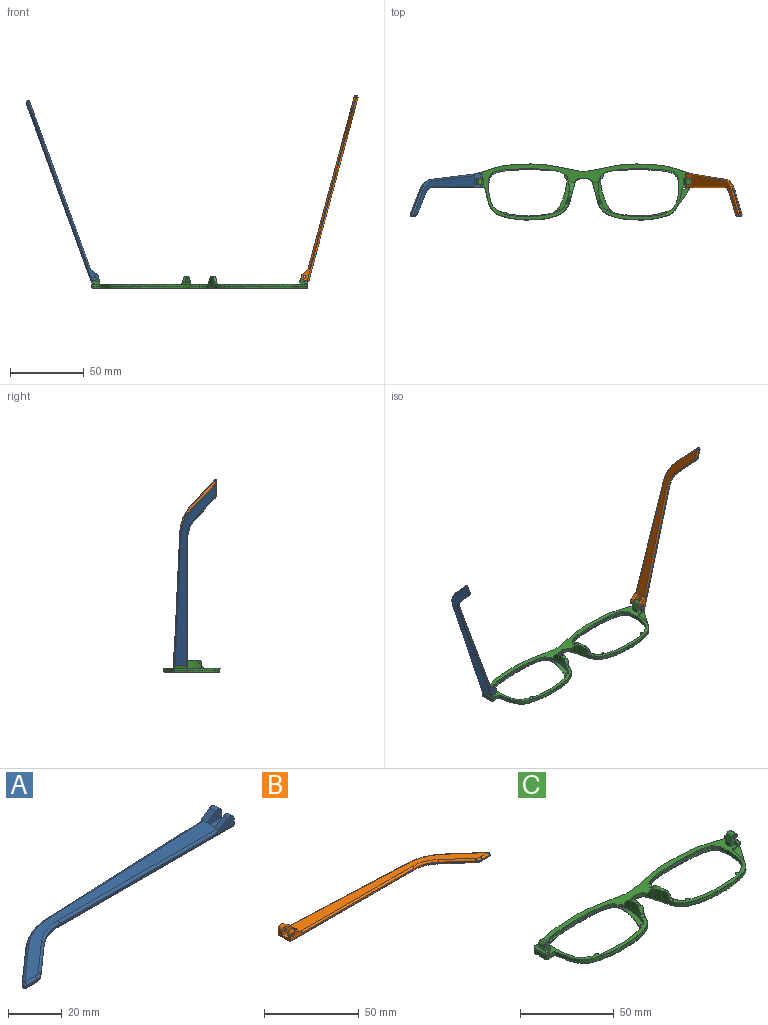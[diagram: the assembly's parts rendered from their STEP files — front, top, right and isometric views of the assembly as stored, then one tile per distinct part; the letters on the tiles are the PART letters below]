
ASSEMBLY  parts=3 mates=2
PART A: 43 faces, bbox 130.2x29.5x5.9 mm
  f0: plane 9.62x3.72mm, normal (1,0,0), area 24.7mm2, adj f1,f3,f4,f5,f10,f16,f18,f28
  f1: cylinder r=2.2mm len=3.45mm, axis (0,-1,0), area 11mm2, adj f0,f2,f4,f37
  f2: plane 6.01x3.91mm, normal (-0.55,0,0.84), area 12.7mm2, adj f1,f4,f9,f19,f37
  f3: plane 2.26x0.1mm, normal (0,0,1), area 0.1mm2, adj f0,f5,f18
  f4: plane 92.1x4.9mm, normal (0,-1,0), area 79.9mm2, adj f0,f1,f2,f14,f19,f36,f42
  f5: plane 93.42x4.13mm, normal (-0.04,1,0), area 64.8mm2, adj f0,f3,f11,f15,f17,f27,f28
  f6: plane 17.82x15.72mm, normal (-0.66,0.75,0), area 14.3mm2, adj f11,f12,f25,f30
  f7: plane 5.46x0.6mm, normal (0,-1,0), area 3.3mm2, adj f12,f13,f23,f32
  f8: plane 14.99x13.23mm, normal (0.66,-0.75,0), area 12mm2, adj f13,f14,f21,f34
  f9: plane 121.18x26.73mm, normal (0,0,1), area 627.7mm2, adj f2,f17,f19,f20,f21,f22,f23,f25
  f10: plane 129.1x27.08mm, normal (0,0,-1), area 686.5mm2, adj f0,f28,f29,f30,f32,f33,f34,f35
  f11: cylinder r=30mm len=18.52mm, axis (0,0,-1), area 12.2mm2, adj f5,f6,f26,f29
  f12: cylinder r=1mm len=1.75mm, axis (0,0,-1), area 1.5mm2, adj f6,f7,f24,f31
  f13: cylinder r=5mm len=3.31mm, axis (0,0,-1), area 2.2mm2, adj f7,f8,f22,f33
  f14: cylinder r=20mm len=13.23mm, axis (0,0,1), area 8.7mm2, adj f4,f8,f20,f35
  f15: plane 5.66x0.25mm, normal (0,0,-1), area 0.7mm2, adj f5,f17,f18
  f16: cylinder r=2.2mm len=3.45mm, axis (0,-1,0), area 14.8mm2, adj f0,f17,f18,f38
  f17: plane 6.01x3.91mm, normal (-0.55,0,0.84), area 16.9mm2, adj f5,f9,f15,f16,f18,f27,f38
  f18: plane 7.92x3.3mm, normal (0,1,0), area 15.9mm2, adj f0,f3,f15,f16,f17,f41
  f19: cylinder r=1mm len=84.18mm, axis (-1,0,0), area 131.4mm2, adj f2,f4,f9,f20
  f20: torus R=21mm, axis (0,0,1), area 23.1mm2, adj f9,f14,f19,f21
  f21: cylinder r=1mm len=15.65mm, axis (-0.75,-0.66,0), area 31.4mm2, adj f8,f9,f20,f22
  f22: torus R=4mm, axis (0,0,1), area 5.3mm2, adj f9,f13,f21,f23
  f23: cylinder r=1mm len=5.46mm, axis (-1,0,0), area 8.6mm2, adj f7,f9,f22,f24
  f24: sphere r=1mm, area 2.4mm2, adj f12,f23,f25
  f25: cylinder r=1mm len=18.48mm, axis (0.75,0.66,0), area 37.3mm2, adj f6,f9,f24,f26
  f26: torus R=29mm, axis (0,0,1), area 31.6mm2, adj f9,f11,f25,f27
  f27: cylinder r=1mm len=85.5mm, axis (1,0.04,0), area 133.5mm2, adj f5,f9,f17,f26
  f28: cylinder r=1mm len=93.46mm, axis (-1,-0.04,0), area 146.9mm2, adj f0,f5,f10,f29
  f29: torus R=29mm, axis (0,0,1), area 31.6mm2, adj f10,f11,f28,f30
  f30: cylinder r=1mm len=18.48mm, axis (-0.75,-0.66,0), area 37.3mm2, adj f6,f10,f29,f31
  f31: sphere r=1mm, area 2.4mm2, adj f12,f30,f32
  f32: cylinder r=1mm len=5.46mm, axis (1,0,0), area 8.6mm2, adj f7,f10,f31,f33
  f33: torus R=4mm, axis (0,0,1), area 5.3mm2, adj f10,f13,f32,f34
  f34: cylinder r=1mm len=15.65mm, axis (0.75,0.66,0), area 31.4mm2, adj f8,f10,f33,f35
  f35: torus R=21mm, axis (0,0,1), area 23.1mm2, adj f10,f14,f34,f36
  f36: cylinder r=1mm len=92.1mm, axis (1,0,0), area 144.7mm2, adj f0,f4,f10,f35
  f37: plane 7.92x4.7mm, normal (0,1,0), area 27mm2, adj f0,f1,f2,f39,f40,f42
  f38: plane 7.92x4.7mm, normal (0,-1,0), area 27mm2, adj f0,f16,f17,f39,f40,f41
  f39: plane 7.92x4.1mm, normal (0,0,1), area 32.5mm2, adj f0,f37,f38,f40
  f40: plane 4.1x1.4mm, normal (1,0,0), area 5.7mm2, adj f9,f37,f38,f39
  f41: cylinder r=0.5mm len=3.1mm, axis (0,-1,0), area 9.7mm2, adj f18,f38
  f42: cylinder r=0.5mm len=2.3mm, axis (0,-1,0), area 7.2mm2, adj f4,f37
PART B: 43 faces, bbox 130.2x29.5x5.9 mm
  f0: plane 9.62x3.72mm, normal (-1,0,0), area 24.7mm2, adj f1,f3,f4,f5,f10,f16,f18,f28
  f1: cylinder r=2.2mm len=3.45mm, axis (0,-1,0), area 11mm2, adj f0,f2,f4,f37
  f2: plane 6.01x3.91mm, normal (0.55,0,0.84), area 12.7mm2, adj f1,f4,f9,f19,f37
  f3: plane 2.26x0.1mm, normal (0,0,1), area 0.1mm2, adj f0,f5,f18
  f4: plane 92.1x4.9mm, normal (0,-1,0), area 78.2mm2, adj f0,f1,f2,f14,f19,f36,f42
  f5: plane 93.42x4.13mm, normal (0.04,1,0), area 64.8mm2, adj f0,f3,f11,f15,f17,f27,f28
  f6: plane 17.82x15.72mm, normal (0.66,0.75,0), area 14.3mm2, adj f11,f12,f25,f30
  f7: plane 5.46x0.6mm, normal (0,-1,0), area 3.3mm2, adj f12,f13,f23,f32
  f8: plane 14.99x13.23mm, normal (-0.66,-0.75,0), area 12mm2, adj f13,f14,f21,f34
  f9: plane 121.18x26.73mm, normal (0,0,1), area 627.7mm2, adj f2,f17,f19,f20,f21,f22,f23,f25
  f10: plane 129.1x27.08mm, normal (0,0,-1), area 686.5mm2, adj f0,f28,f29,f30,f32,f33,f34,f35
  f11: cylinder r=30mm len=18.52mm, axis (0,0,-1), area 12.2mm2, adj f5,f6,f26,f29
  f12: cylinder r=1mm len=1.75mm, axis (0,0,-1), area 1.5mm2, adj f6,f7,f24,f31
  f13: cylinder r=5mm len=3.31mm, axis (0,0,-1), area 2.2mm2, adj f7,f8,f22,f33
  f14: cylinder r=20mm len=13.23mm, axis (0,0,1), area 8.7mm2, adj f4,f8,f20,f35
  f15: plane 5.66x0.25mm, normal (0,0,-1), area 0.7mm2, adj f5,f17,f18
  f16: cylinder r=2.2mm len=3.45mm, axis (0,-1,0), area 14.8mm2, adj f0,f17,f18,f38
  f17: plane 6.01x3.91mm, normal (0.55,0,0.84), area 16.9mm2, adj f5,f9,f15,f16,f18,f27,f38
  f18: plane 7.92x3.3mm, normal (0,1,0), area 14.3mm2, adj f0,f3,f15,f16,f17,f41
  f19: cylinder r=1mm len=84.18mm, axis (1,0,0), area 131.4mm2, adj f2,f4,f9,f20
  f20: torus R=21mm, axis (0,0,1), area 23.1mm2, adj f9,f14,f19,f21
  f21: cylinder r=1mm len=15.65mm, axis (0.75,-0.66,0), area 31.4mm2, adj f8,f9,f20,f22
  f22: torus R=4mm, axis (0,0,1), area 5.3mm2, adj f9,f13,f21,f23
  f23: cylinder r=1mm len=5.46mm, axis (1,0,0), area 8.6mm2, adj f7,f9,f22,f24
  f24: sphere r=1mm, area 2.4mm2, adj f12,f23,f25
  f25: cylinder r=1mm len=18.48mm, axis (-0.75,0.66,0), area 37.3mm2, adj f6,f9,f24,f26
  f26: torus R=29mm, axis (0,0,1), area 31.6mm2, adj f9,f11,f25,f27
  f27: cylinder r=1mm len=85.5mm, axis (-1,0.04,0), area 133.5mm2, adj f5,f9,f17,f26
  f28: cylinder r=1mm len=93.46mm, axis (1,-0.04,0), area 146.9mm2, adj f0,f5,f10,f29
  f29: torus R=29mm, axis (0,0,1), area 31.6mm2, adj f10,f11,f28,f30
  f30: cylinder r=1mm len=18.48mm, axis (0.75,-0.66,0), area 37.3mm2, adj f6,f10,f29,f31
  f31: sphere r=1mm, area 2.4mm2, adj f12,f30,f32
  f32: cylinder r=1mm len=5.46mm, axis (-1,0,0), area 8.6mm2, adj f7,f10,f31,f33
  f33: torus R=4mm, axis (0,0,1), area 5.3mm2, adj f10,f13,f32,f34
  f34: cylinder r=1mm len=15.65mm, axis (-0.75,0.66,0), area 31.4mm2, adj f8,f10,f33,f35
  f35: torus R=21mm, axis (0,0,1), area 23.1mm2, adj f10,f14,f34,f36
  f36: cylinder r=1mm len=92.1mm, axis (-1,0,0), area 144.7mm2, adj f0,f4,f10,f35
  f37: plane 7.92x4.7mm, normal (0,1,0), area 25.4mm2, adj f0,f1,f2,f39,f40,f42
  f38: plane 7.92x4.7mm, normal (0,-1,0), area 25.4mm2, adj f0,f16,f17,f39,f40,f41
  f39: plane 7.92x4.1mm, normal (0,0,1), area 32.5mm2, adj f0,f37,f38,f40
  f40: plane 4.1x1.4mm, normal (-1,0,0), area 5.7mm2, adj f9,f37,f38,f39
  f41: cylinder r=0.88mm len=3.1mm, axis (0,-1,0), area 17mm2, adj f18,f38
  f42: cylinder r=0.88mm len=2.3mm, axis (0,-1,0), area 12.6mm2, adj f4,f37
PART C: 116 faces, bbox 148.1x38.6x17.8 mm
  f0: plane 9.74x2.07mm, normal (0,0,1), area 0.2mm2, adj f1,f115
  f1: extruded ~54.55x32.6mm, area 138.1mm2, adj f0,f2,f103,f104,f105,f106,f107,f108
  f2: extruded ~54.55x32.6mm, area 127.7mm2, adj f1,f3,f103
  f3: plane 54.78x32.76mm, normal (0,0,1), area 120.4mm2, adj f2,f4
  f4: bspline ~55.13x33.28mm, area 230.1mm2, adj f3,f5,f102,f103
  f5: bspline ~72.92x29.28mm, area 158.8mm2, adj f4,f6,f69,f101,f102
  f6: bspline ~72.92x29.28mm, area 158.8mm2, adj f5,f7,f67,f68,f102
  f7: extruded ~73.28x38.08mm, area 259.3mm2, adj f6,f8,f9,f10,f29,f30,f31,f32
  f8: extruded ~0.11x0.03mm, area 0mm2, adj f7,f66
  f9: extruded ~4.12x1.97mm, area 6.9mm2, adj f7,f66
  f10: plane 5.35x2.29mm, normal (0,0,1), area 6.4mm2, adj f7,f11,f28,f29,f66
  f11: bspline ~7.24x7.24mm, area 12.1mm2, adj f10,f12,f27,f28,f29,f30
  f12: bspline ~3.15x1.97mm, area 4.7mm2, adj f11,f13,f14,f31,f112
  f13: cylinder r=1.54mm len=1.03mm, axis (1,0,0), area 0.1mm2, adj f12,f27,f30
  f14: extruded ~54.55x32.6mm, area 138.1mm2, adj f12,f15,f17,f18,f19,f20,f21,f22
  f15: extruded ~54.55x32.6mm, area 127.7mm2, adj f14,f16,f17
  f16: plane 54.78x32.76mm, normal (0,0,1), area 120.4mm2, adj f15,f67
  f17: extruded ~18.85x7.36mm, area 43.3mm2, adj f14,f15,f67,f112
  f18: plane 1.82x1.47mm, normal (0,0,-1), area 1.5mm2, adj f14,f19
  f19: cylinder r=1mm len=1.82mm, axis (0,0,1), area 1.5mm2, adj f14,f18,f112
  f20: plane 3.16x2.48mm, normal (0,0,-1), area 4.2mm2, adj f14,f21
  f21: cylinder r=2mm len=3.15mm, axis (0,0,1), area 2.4mm2, adj f14,f20,f112
  f22: plane 9.74x2.07mm, normal (0,0,1), area 0.2mm2, adj f14,f28
  f23: plane 2.48x1.81mm, normal (0,0,-1), area 2.6mm2, adj f14,f24
  f24: cylinder r=1.3mm len=2.47mm, axis (0,0,1), area 2mm2, adj f14,f23,f112
  f25: plane 2.52x1.67mm, normal (0,0,-1), area 2.6mm2, adj f14,f26
  f26: cylinder r=1.3mm len=2.51mm, axis (0,0,1), area 2mm2, adj f14,f25,f112
  f27: plane 0.42x0.26mm, normal (0,-1,0), area 0mm2, adj f11,f13,f30
  f28: extruded ~9.47x5mm, area 42.8mm2, adj f10,f11,f14,f22,f66
  f29: extruded ~5x4.22mm, area 20.5mm2, adj f7,f10,f11,f30
  f30: bspline ~2.15x0.76mm, area 0.4mm2, adj f7,f11,f13,f27,f29,f31
  f31: bspline ~1.76x0.83mm, area 0.4mm2, adj f7,f12,f30,f32
  f32: bspline ~62.39x22.31mm, area 24.4mm2, adj f7,f31,f33,f112
  f33: plane 2.36x2.31mm, normal (1,0,0), area 4.9mm2, adj f7,f32,f34,f50,f51,f52,f112
  f34: plane 2.76x2.53mm, normal (0,-1,0), area 3.9mm2, adj f33,f35,f49,f50,f53
  f35: cone r=1mm half-angle=20deg, axis (0,0,1), area 2.3mm2, adj f34,f36,f49,f112
  f36: plane 7.67x1.6mm, normal (-0.94,0,-0.34), area 13mm2, adj f35,f37,f49,f112
  f37: cylinder r=1mm len=2.28mm, axis (0.34,0,-0.94), area 3mm2, adj f36,f38,f49,f112
  f38: plane 2.1x1.68mm, normal (0,1,0), area 2.8mm2, adj f37,f39,f49,f50,f112
  f39: plane 3.3x2.1mm, normal (1,0,0), area 6.9mm2, adj f38,f40,f50,f112
  f40: plane 6.97x5.07mm, normal (0,1,0), area 22.7mm2, adj f39,f41,f42,f43,f44,f45,f46,f47
  f41: cylinder r=1.98mm len=4mm, axis (0,1,0), area 12.4mm2, adj f40,f42,f47,f51
  f42: plane 4x0.01mm, normal (-0.34,0,0.94), area 0.1mm2, adj f40,f41,f43,f51
  f43: cylinder r=1.98mm len=4mm, axis (0,-1,0), area 12.4mm2, adj f40,f42,f44,f51
  f44: plane 4x2.21mm, normal (-0.94,0,-0.34), area 9.4mm2, adj f40,f43,f50,f51
  f45: plane 4x2.36mm, normal (1,0,0), area 9.5mm2, adj f40,f46,f52,f112
  f46: plane 4x0.02mm, normal (-0.34,0,0.94), area 0.1mm2, adj f40,f45,f47
  f47: plane 4x3.31mm, normal (0.94,0,0.34), area 14.1mm2, adj f40,f41,f46,f51
  f48: cylinder r=0.88mm len=4mm, axis (0,-1,0), area 22mm2, adj f40,f51
  f49: plane 9.71x1.44mm, normal (-0.34,0,0.94), area 13.9mm2, adj f34,f35,f36,f37,f38,f50
  f50: plane 9.65x1.24mm, normal (0,0,1), area 8.2mm2, adj f33,f34,f38,f39,f40,f44,f49,f51
  f51: plane 5.77x5.07mm, normal (0,-1,0), area 17mm2, adj f33,f41,f42,f43,f44,f47,f48,f50
  f52: plane 3.2x2.36mm, normal (0,-1,0), area 5.7mm2, adj f33,f45,f51,f112
  f53: plane 1.22x0.04mm, normal (0,0,1), area 0mm2, adj f7,f34,f112
  f54: extruded ~35.98x5.06mm, area 72.9mm2, adj f7,f55,f60,f112
  f55: bspline ~38.4x6.08mm, area 57.2mm2, adj f54,f56,f61,f102
  f56: bspline ~38.4x6.08mm, area 57.2mm2, adj f55,f57,f60,f102
  f57: bspline ~44.95x7.5mm, area 58.9mm2, adj f56,f58,f69,f102
  f58: bspline ~1.05x1mm, area 0.7mm2, adj f57,f59,f69
  f59: bspline ~8.77x1.22mm, area 12.6mm2, adj f58,f69,f101,f102
  f60: extruded ~35.98x5.06mm, area 72.9mm2, adj f54,f56,f69,f112
  f61: bspline ~44.95x7.5mm, area 58.9mm2, adj f7,f55,f62,f102
  f62: bspline ~1.05x1mm, area 0.8mm2, adj f7,f61,f63
  f63: bspline ~8.77x1.22mm, area 12.6mm2, adj f7,f62,f68,f102
  f64: bspline ~6.56x3.87mm, area 2.3mm2, adj f7,f65,f66,f112
  f65: bspline ~6.56x3.87mm, area 2.3mm2, adj f64,f69,f108,f112
  f66: bspline ~15.41x15.33mm, area 32.8mm2, adj f7,f8,f9,f10,f14,f28,f64,f112
  f67: bspline ~55.13x33.28mm, area 230.1mm2, adj f6,f16,f17,f102
  f68: bspline ~1x1mm, area 0.8mm2, adj f6,f7,f63
  f69: extruded ~73.28x38.08mm, area 259.3mm2, adj f5,f7,f57,f58,f59,f60,f65,f70
  f70: extruded ~4.12x1.97mm, area 6.9mm2, adj f69,f108
  f71: plane 5.35x2.29mm, normal (0,0,1), area 6.4mm2, adj f69,f72,f75,f108,f115
  f72: bspline ~7.24x7.24mm, area 12.1mm2, adj f71,f73,f75,f76,f109,f115
  f73: plane 0.42x0.26mm, normal (0,-1,0), area 0mm2, adj f72,f74,f76
  f74: cylinder r=1.54mm len=1.03mm, axis (-1,0,0), area 0.1mm2, adj f73,f76,f109
  f75: extruded ~5x4.22mm, area 20.5mm2, adj f69,f71,f72,f76
  f76: bspline ~2.15x0.76mm, area 0.4mm2, adj f69,f72,f73,f74,f75,f77
  f77: bspline ~1.76x0.83mm, area 0.4mm2, adj f69,f76,f78,f109
  f78: bspline ~62.39x22.31mm, area 24.4mm2, adj f69,f77,f79,f112
  f79: plane 2.36x2.31mm, normal (-1,0,0), area 4.9mm2, adj f69,f78,f80,f96,f97,f98,f112
  f80: plane 3.2x2.36mm, normal (0,-1,0), area 5.7mm2, adj f79,f81,f96,f112
  f81: plane 4x2.36mm, normal (-1,0,0), area 9.5mm2, adj f80,f82,f95,f112
  f82: plane 6.97x5.07mm, normal (0,1,0), area 22.7mm2, adj f81,f83,f89,f90,f91,f92,f93,f94
  f83: plane 3.3x2.1mm, normal (-1,0,0), area 6.9mm2, adj f82,f84,f97,f112
  f84: plane 2.1x1.68mm, normal (0,1,0), area 2.8mm2, adj f83,f85,f88,f97,f112
  f85: cylinder r=1mm len=2.28mm, axis (-0.34,0,-0.94), area 3mm2, adj f84,f86,f88,f112
  f86: plane 7.67x1.6mm, normal (0.94,0,-0.34), area 13mm2, adj f85,f87,f88,f112
  f87: cone r=1mm half-angle=20deg, axis (0,0,1), area 2.3mm2, adj f86,f88,f98,f112
  f88: plane 9.71x1.44mm, normal (0.34,0,0.94), area 13.9mm2, adj f84,f85,f86,f87,f97,f98
  f89: plane 4x2.21mm, normal (0.94,0,-0.34), area 9.4mm2, adj f82,f90,f96,f97
  f90: cylinder r=1.98mm len=4mm, axis (0,-1,0), area 12.4mm2, adj f82,f89,f91,f96
  f91: plane 4x0.01mm, normal (0.34,0,0.94), area 0.1mm2, adj f82,f90,f92,f96
  f92: cylinder r=1.98mm len=4mm, axis (0,1,0), area 12.4mm2, adj f82,f91,f93,f96
  f93: plane 4x3.31mm, normal (-0.94,0,0.34), area 14.1mm2, adj f82,f92,f95,f96
  f94: cylinder r=0.88mm len=4mm, axis (0,-1,0), area 22mm2, adj f82,f96
  f95: plane 4x0.02mm, normal (0.34,0,0.94), area 0.1mm2, adj f81,f82,f93
  f96: plane 5.77x5.06mm, normal (0,-1,0), area 17mm2, adj f79,f80,f89,f90,f91,f92,f93,f94
  f97: plane 9.65x1.24mm, normal (0,0,1), area 8.2mm2, adj f79,f82,f83,f84,f88,f89,f96,f98
  f98: plane 2.76x2.53mm, normal (0,-1,0), area 3.9mm2, adj f79,f87,f88,f97,f99
  f99: plane 1.22x0.04mm, normal (0,0,1), area 0mm2, adj f69,f98,f112
  f100: extruded ~0.11x0.03mm, area 0mm2, adj f69,f108
  f101: bspline ~1x1mm, area 0.8mm2, adj f5,f59,f69
  f102: plane 144.79x36.11mm, normal (0,0,-1), area 646.3mm2, adj f4,f5,f6,f55,f56,f57,f59,f61
  f103: extruded ~18.85x7.36mm, area 43.3mm2, adj f1,f2,f4,f112
  f104: plane 1.82x1.47mm, normal (0,0,-1), area 1.5mm2, adj f1,f105
  f105: cylinder r=1mm len=1.82mm, axis (0,0,1), area 1.5mm2, adj f1,f104,f112
  f106: plane 3.16x2.48mm, normal (0,0,-1), area 4.2mm2, adj f1,f107
  f107: cylinder r=2mm len=3.15mm, axis (0,0,1), area 2.4mm2, adj f1,f106,f112
  f108: bspline ~15.41x15.33mm, area 32.8mm2, adj f1,f65,f69,f70,f71,f100,f112,f115
  f109: bspline ~3.15x1.97mm, area 4.7mm2, adj f1,f72,f74,f77,f112
  f110: plane 2.48x1.81mm, normal (0,0,-1), area 2.6mm2, adj f1,f111
  f111: cylinder r=1.3mm len=2.47mm, axis (0,0,1), area 2mm2, adj f1,f110,f112
  f112: plane 147.43x38.06mm, normal (0,0,1), area 907.2mm2, adj f1,f7,f12,f14,f17,f19,f21,f24
  f113: cylinder r=1.3mm len=2.51mm, axis (0,0,1), area 2mm2, adj f1,f112,f114
  f114: plane 2.52x1.67mm, normal (0,0,-1), area 2.6mm2, adj f1,f113
  f115: extruded ~9.47x5mm, area 42.8mm2, adj f0,f1,f71,f72,f108
PLACE A rot(axis=(0,1,0),70deg) t=(-84.77,-5.75,56)mm
PLACE B rot(axis=(0,-1,0),75deg) t=(68.2,-5.75,-61.61)mm
PLACE C t=(10.15,-1.13,-5.77)mm
MATE revolute A.f1 <-> C.f41  axis (0,-1,0) through (-60.89,2.72,1.22)mm
MATE revolute B.f41 <-> C.f90  axis (0,-1,0) through (81.2,2.72,1.21)mm
